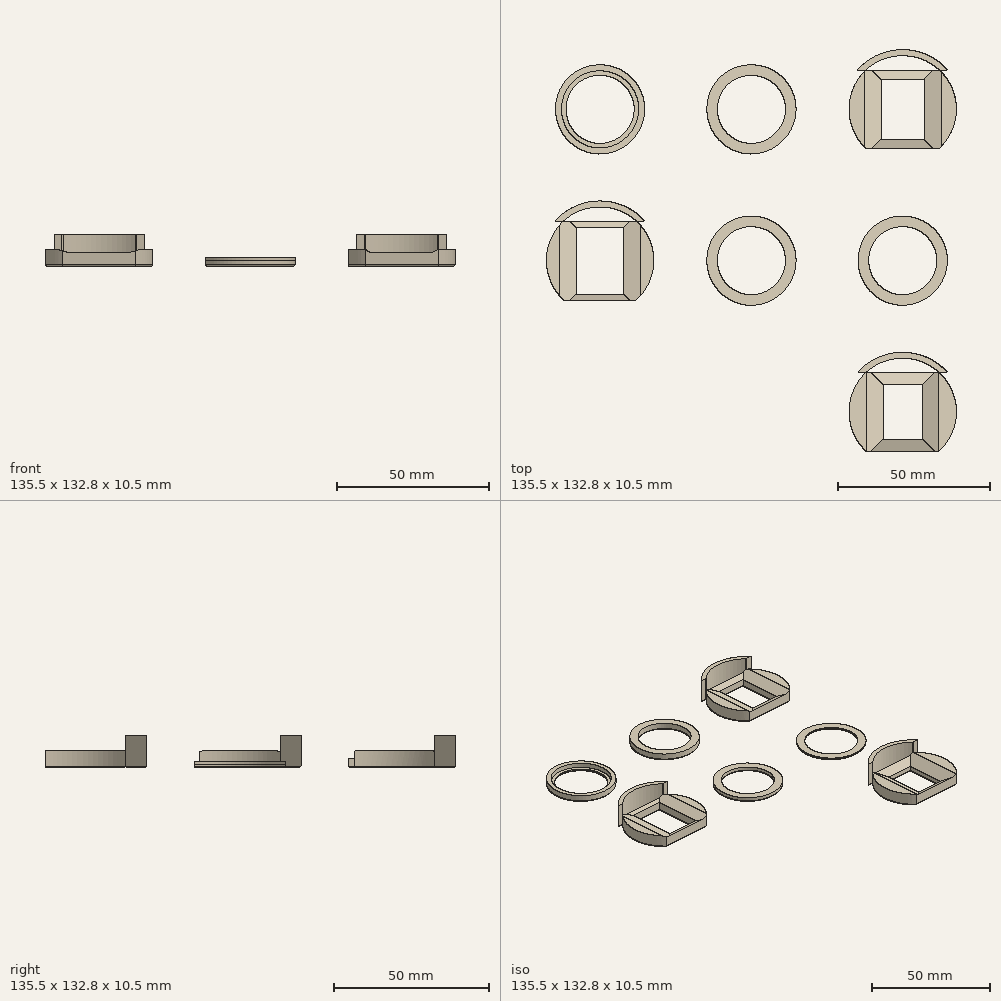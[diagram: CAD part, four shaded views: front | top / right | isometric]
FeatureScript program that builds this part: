
annotation { "Feature Type Name" : "Feature", "Feature Type Description" : "" }
export const myFeature = defineFeature(function(context is Context, id is Id, definition is map)
    precondition{}
    {
        {
            var Q0;
            Q0=qCreatedBy(makeId("Top.planeOp"),FACE);
            var sketch = newSketch(context, id + "F0", { "sketchPlane" : qUnion([Q0])});
            skCircle(sketch, "E0", {"center": v(-61.15, 61.18) * mm, "radius": 11.25 * mm});
            skCircle(sketch, "E1", {"center": v(-61.15, 61.18) * mm, "radius": 14.75 * mm});
            skLineSegment(sketch, "E2.bottom", {"start": v(-69.03, 22.18) * mm, "end": v(-53.28, 22.18) * mm});
            skLineSegment(sketch, "E2.top", {"start": v(-69.03, 0.18) * mm, "end": v(-53.28, 0.18) * mm});
            skLineSegment(sketch, "E2.left", {"start": v(-69.03, 22.18) * mm, "end": v(-69.03, 0.18) * mm});
            skLineSegment(sketch, "E2.right", {"start": v(-53.28, 22.18) * mm, "end": v(-53.28, 0.18) * mm});
            skLineSegment(sketch, "E3", {"start": v(-69.03, 0.18) * mm, "end": v(-53.28, 22.18) * mm, "construction": true});
            skCircle(sketch, "E4", {"center": v(-61.15, 11.18) * mm, "radius": 17.75 * mm});
            skCircle(sketch, "E5", {"center": v(-61.15, 11.18) * mm, "radius": 19.75 * mm});
            skCircle(sketch, "E6", {"center": v(-61.15, 61.18) * mm, "radius": 12.75 * mm});
            skLineSegment(sketch, "E7", {"start": v(-76.02, 24.18) * mm, "end": v(-46.29, 24.18) * mm});
            skLineSegment(sketch, "E8", {"start": v(-76.02, -1.82) * mm, "end": v(-46.29, -1.82) * mm});
            skCircle(sketch, "E9", {"center": v(-11.15, 61.18) * mm, "radius": 11.25 * mm});
            skCircle(sketch, "E10", {"center": v(-11.15, 61.18) * mm, "radius": 14.75 * mm});
            skCircle(sketch, "E11", {"center": v(-11.15, 11.18) * mm, "radius": 11.25 * mm});
            skCircle(sketch, "E12", {"center": v(-11.15, 11.18) * mm, "radius": 14.75 * mm});
            skCircle(sketch, "E13", {"center": v(38.85, 11.18) * mm, "radius": 11.25 * mm});
            skCircle(sketch, "E14", {"center": v(38.85, 11.18) * mm, "radius": 14.75 * mm});
            skLineSegment(sketch, "E15.bottom", {"start": v(31.69, 71.18) * mm, "end": v(46, 71.18) * mm});
            skLineSegment(sketch, "E15.top", {"start": v(31.69, 51.18) * mm, "end": v(46, 51.18) * mm});
            skLineSegment(sketch, "E15.left", {"start": v(31.69, 71.18) * mm, "end": v(31.69, 51.18) * mm});
            skLineSegment(sketch, "E15.right", {"start": v(46, 71.18) * mm, "end": v(46, 51.18) * mm});
            skLineSegment(sketch, "E16", {"start": v(31.69, 51.18) * mm, "end": v(46, 71.18) * mm, "construction": true});
            skCircle(sketch, "E17", {"center": v(38.85, 61.18) * mm, "radius": 17.75 * mm});
            skCircle(sketch, "E18", {"center": v(38.85, 61.18) * mm, "radius": 19.75 * mm});
            skLineSegment(sketch, "E19", {"start": v(23.98, 74.18) * mm, "end": v(53.71, 74.18) * mm});
            skLineSegment(sketch, "E20", {"start": v(23.98, 48.18) * mm, "end": v(53.71, 48.18) * mm});
            skLineSegment(sketch, "E21.bottom", {"start": v(32.4, -29.82) * mm, "end": v(45.29, -29.82) * mm});
            skLineSegment(sketch, "E21.top", {"start": v(32.4, -47.82) * mm, "end": v(45.29, -47.82) * mm});
            skLineSegment(sketch, "E21.left", {"start": v(32.4, -29.82) * mm, "end": v(32.4, -47.82) * mm});
            skLineSegment(sketch, "E21.right", {"start": v(45.29, -29.82) * mm, "end": v(45.29, -47.82) * mm});
            skLineSegment(sketch, "E22", {"start": v(32.4, -47.82) * mm, "end": v(45.29, -29.82) * mm, "construction": true});
            skCircle(sketch, "E23", {"center": v(38.85, -38.82) * mm, "radius": 17.75 * mm});
            skCircle(sketch, "E24", {"center": v(38.85, -38.82) * mm, "radius": 19.75 * mm});
            skLineSegment(sketch, "E25", {"start": v(23.98, -25.82) * mm, "end": v(53.71, -25.82) * mm});
            skLineSegment(sketch, "E26", {"start": v(23.98, -51.82) * mm, "end": v(53.71, -51.82) * mm});
            skSolve(sketch);
        }
        {
            var Q0;
            Q0=makeQuery(id+"F0.imprint","IMPRINT",FACE,{"disambiguationData":[TD([[makeQuery(id+"F0.imprint","IMPRINT",EDGE,{"derivedFrom":sQuery(id+"F0.wireOp",EDGE,"E0")}),-1.0]])]});
            extrude(context, id + "F1", {"entities" : qUnion([Q0]), "depth" : 1 * mm, "offsetDistance" : 25 * mm});
        }
        {
            var Q0;
            Q0=makeQuery(id+"F0.imprint","IMPRINT",FACE,{"disambiguationData":[TD([[makeQuery(id+"F0.imprint","IMPRINT",EDGE,{"derivedFrom":sQuery(id+"F0.wireOp",EDGE,"E1")}),1.0]])]});
            extrude(context, id + "F2", {"entities" : qUnion([Q0]), "operationType" : NewBodyOperationType.ADD, "depth" : 3 * mm, "offsetDistance" : 25 * mm});
        }
        {
            var Q0;
            Q0=makeQuery(id+"F0.imprint","IMPRINT",FACE,{"disambiguationData":[TD([[makeQuery(id+"F0.imprint","IMPRINT",EDGE,{"derivedFrom":sQuery(id+"F0.wireOp",EDGE,"E2.bottom")}),1.0]])]});
            var Q1;
            Q1=makeQuery(id+"F0.imprint","IMPRINT",FACE,{"disambiguationData":[TD([[makeQuery(id+"F0.imprint","IMPRINT",EDGE,{"derivedFrom":sQuery(id+"F0.wireOp",EDGE,"E15.bottom")}),1.0]])]});
            var Q2;
            Q2=makeQuery(id+"F0.imprint","IMPRINT",FACE,{"disambiguationData":[TD([[makeQuery(id+"F0.imprint","IMPRINT",EDGE,{"derivedFrom":sQuery(id+"F0.wireOp",EDGE,"E21.bottom")}),1.0]])]});
            extrude(context, id + "F3", {"entities" : qUnion([Q0, Q1, Q2]), "depth" : 5.5 * mm, "offsetDistance" : 25 * mm});
        }
        {
            var Q0;
            {var subQ0=sQuery(id+"F0.wireOp",EDGE,"E7");var subQ1=sQuery(id+"F0.wireOp",EDGE,"E4");var subQ2=makeQuery(id+"F0.imprint","INTERSECT",VERTEX,{"disambiguationData":[OD(0.0)],"derivedFrom":[subQ1,subQ0]});Q0=makeQuery(id+"F0.imprint","IMPRINT",FACE,{"disambiguationData":[TD([[makeQuery(id+"F0.imprint","IMPRINT",EDGE,{"disambiguationData":[TD([[subQ2,-1.0]])],"derivedFrom":subQ1}),-1.0]])]});}
            var Q1;
            {var subQ0=sQuery(id+"F0.wireOp",EDGE,"E7");var subQ1=sQuery(id+"F0.wireOp",EDGE,"E4");var subQ2=makeQuery(id+"F0.imprint","INTERSECT",VERTEX,{"disambiguationData":[OD(1.0)],"derivedFrom":[subQ1,subQ0]});Q1=makeQuery(id+"F0.imprint","IMPRINT",FACE,{"disambiguationData":[TD([[makeQuery(id+"F0.imprint","IMPRINT",EDGE,{"disambiguationData":[TD([[subQ2,1.0]])],"derivedFrom":subQ1}),-1.0]])]});}
            var Q2;
            {var subQ0=sQuery(id+"F0.wireOp",EDGE,"E19");var subQ1=sQuery(id+"F0.wireOp",EDGE,"E17");var subQ2=makeQuery(id+"F0.imprint","INTERSECT",VERTEX,{"disambiguationData":[OD(0.0)],"derivedFrom":[subQ1,subQ0]});Q2=makeQuery(id+"F0.imprint","IMPRINT",FACE,{"disambiguationData":[TD([[makeQuery(id+"F0.imprint","IMPRINT",EDGE,{"disambiguationData":[TD([[subQ2,-1.0]])],"derivedFrom":subQ1}),-1.0]])]});}
            var Q3;
            {var subQ0=sQuery(id+"F0.wireOp",EDGE,"E19");var subQ1=sQuery(id+"F0.wireOp",EDGE,"E17");var subQ2=makeQuery(id+"F0.imprint","INTERSECT",VERTEX,{"disambiguationData":[OD(1.0)],"derivedFrom":[subQ1,subQ0]});Q3=makeQuery(id+"F0.imprint","IMPRINT",FACE,{"disambiguationData":[TD([[makeQuery(id+"F0.imprint","IMPRINT",EDGE,{"disambiguationData":[TD([[subQ2,1.0]])],"derivedFrom":subQ1}),-1.0]])]});}
            var Q4;
            {var subQ0=sQuery(id+"F0.wireOp",EDGE,"E25");var subQ1=sQuery(id+"F0.wireOp",EDGE,"E23");var subQ2=makeQuery(id+"F0.imprint","INTERSECT",VERTEX,{"disambiguationData":[OD(0.0)],"derivedFrom":[subQ1,subQ0]});Q4=makeQuery(id+"F0.imprint","IMPRINT",FACE,{"disambiguationData":[TD([[makeQuery(id+"F0.imprint","IMPRINT",EDGE,{"disambiguationData":[TD([[subQ2,-1.0]])],"derivedFrom":subQ1}),-1.0]])]});}
            var Q5;
            {var subQ0=sQuery(id+"F0.wireOp",EDGE,"E25");var subQ1=sQuery(id+"F0.wireOp",EDGE,"E23");var subQ2=makeQuery(id+"F0.imprint","INTERSECT",VERTEX,{"disambiguationData":[OD(1.0)],"derivedFrom":[subQ1,subQ0]});Q5=makeQuery(id+"F0.imprint","IMPRINT",FACE,{"disambiguationData":[TD([[makeQuery(id+"F0.imprint","IMPRINT",EDGE,{"disambiguationData":[TD([[subQ2,1.0]])],"derivedFrom":subQ1}),-1.0]])]});}
            extrude(context, id + "F4", {"entities" : qUnion([Q0, Q1, Q2, Q3, Q4, Q5]), "operationType" : NewBodyOperationType.ADD, "depth" : 10.5 * mm, "offsetDistance" : 25 * mm});
        }
        {
            var Q0;
            Q0=makeQuery(id+"F0.imprint","IMPRINT",FACE,{"disambiguationData":[TD([[makeQuery(id+"F0.imprint","IMPRINT",EDGE,{"derivedFrom":sQuery(id+"F0.wireOp",EDGE,"E10")}),1.0]])]});
            extrude(context, id + "F5", {"entities" : qUnion([Q0]), "depth" : 3 * mm, "offsetDistance" : 25 * mm});
        }
        {
            var Q0;
            Q0=makeQuery(id+"F0.imprint","IMPRINT",FACE,{"disambiguationData":[TD([[makeQuery(id+"F0.imprint","IMPRINT",EDGE,{"derivedFrom":sQuery(id+"F0.wireOp",EDGE,"E11")}),-1.0]])]});
            extrude(context, id + "F6", {"entities" : qUnion([Q0]), "operationType" : NewBodyOperationType.ADD, "depth" : 2 * mm, "offsetDistance" : 25 * mm});
        }
        {
            var Q0;
            Q0=makeQuery(id+"F0.imprint","IMPRINT",FACE,{"disambiguationData":[TD([[makeQuery(id+"F0.imprint","IMPRINT",EDGE,{"derivedFrom":sQuery(id+"F0.wireOp",EDGE,"E14")}),1.0]])]});
            extrude(context, id + "F7", {"entities" : qUnion([Q0]), "depth" : 1 * mm, "offsetDistance" : 25 * mm});
        }
        {
            var Q0;
            Q0=makeQuery(id+"F3.opExtrude","CAP_EDGE",EDGE,{"disambiguationData":[OSD([sQuery(id+"F0.wireOp",EDGE,"E2.bottom")])],"isStart":false});
            var Q1;
            Q1=makeQuery(id+"F3.opExtrude","CAP_EDGE",EDGE,{"disambiguationData":[OSD([sQuery(id+"F0.wireOp",EDGE,"E2.right")])],"isStart":false});
            var Q2;
            Q2=makeQuery(id+"F3.opExtrude","CAP_EDGE",EDGE,{"disambiguationData":[OSD([sQuery(id+"F0.wireOp",EDGE,"E2.top")])],"isStart":false});
            var Q3;
            Q3=makeQuery(id+"F3.opExtrude","CAP_EDGE",EDGE,{"disambiguationData":[OSD([sQuery(id+"F0.wireOp",EDGE,"E2.left")])],"isStart":false});
            chamfer(context, id + "F8", {"entities" : qUnion([Q0, Q1, Q2, Q3]), "chamferType" : ChamferType.TWO_OFFSETS, "width1" : 1.6 * mm, "oppositeDirection" : false, "width2" : 5.5 * mm, "tangentPropagation" : true});
        }
        {
            var Q0;
            {var subQ0=sQuery(id+"F0.wireOp",EDGE,"E8");var subQ1=sQuery(id+"F0.wireOp",EDGE,"E5");var subQ2=makeQuery(id+"F0.imprint","INTERSECT",VERTEX,{"disambiguationData":[OD(1.0)],"derivedFrom":[subQ1,subQ0]});var subQ3=sQuery(id+"F0.wireOp",EDGE,"E4");var subQ5=sQuery(id+"F0.wireOp",EDGE,"E7");var subQ6=makeQuery(id+"F0.imprint","INTERSECT",VERTEX,{"disambiguationData":[OD(1.0)],"derivedFrom":[subQ1,subQ5]});var subQ7=makeQuery(id+"F0.imprint","INTERSECT",VERTEX,{"disambiguationData":[OD(1.0)],"derivedFrom":[subQ3,subQ5]});var subQ8=makeQuery(id+"F0.imprint","INTERSECT",VERTEX,{"disambiguationData":[OD(0.0)],"derivedFrom":[subQ1,subQ0]});var subQ10=makeQuery(id+"F0.imprint","INTERSECT",VERTEX,{"disambiguationData":[OD(0.0)],"derivedFrom":[subQ1,subQ5]});var subQ11=makeQuery(id+"F0.imprint","INTERSECT",VERTEX,{"disambiguationData":[OD(0.0)],"derivedFrom":[subQ3,subQ5]});Q0=makeQuery(id+"F4.boolean.opBoolean","MERGE",FACE,{"derivedFrom":[makeQuery(id+"F3.opExtrude","CAP_FACE",FACE,{"disambiguationData":[OSD([sQuery(id+"F0.wireOp",EDGE,"E2.bottom"),sQuery(id+"F0.wireOp",EDGE,"E2.top"),sQuery(id+"F0.wireOp",EDGE,"E2.left"),sQuery(id+"F0.wireOp",EDGE,"E2.right"),subQ3,subQ5,subQ0])],"isStart":true}),makeQuery(id+"F4.opExtrude","CAP_FACE",FACE,{"disambiguationData":[OSD([subQ3,subQ1,subQ5,subQ0]),TDD([makeQuery(id+"F0.imprint","IMPRINT",EDGE,{"disambiguationData":[TD([[subQ11,-1.0]])],"derivedFrom":subQ3}),makeQuery(id+"F0.imprint","IMPRINT",EDGE,{"disambiguationData":[TD([[subQ10,-1.0]])],"derivedFrom":subQ1}),makeQuery(id+"F0.imprint","IMPRINT",EDGE,{"disambiguationData":[TD([[subQ10,-1.0]])],"derivedFrom":subQ5}),makeQuery(id+"F0.imprint","IMPRINT",EDGE,{"disambiguationData":[TD([[subQ8,-1.0]])],"derivedFrom":subQ0})])],"isStart":true}),makeQuery(id+"F4.opExtrude","CAP_FACE",FACE,{"disambiguationData":[OSD([subQ3,subQ1,subQ5,subQ0]),TDD([makeQuery(id+"F0.imprint","IMPRINT",EDGE,{"disambiguationData":[TD([[subQ7,1.0]])],"derivedFrom":subQ3}),makeQuery(id+"F0.imprint","IMPRINT",EDGE,{"disambiguationData":[TD([[subQ6,1.0]])],"derivedFrom":subQ1}),makeQuery(id+"F0.imprint","IMPRINT",EDGE,{"disambiguationData":[TD([[subQ6,1.0]])],"derivedFrom":subQ5}),makeQuery(id+"F0.imprint","IMPRINT",EDGE,{"disambiguationData":[TD([[subQ2,1.0]])],"derivedFrom":subQ0})])],"isStart":true})]});}
            var Q1;
            {var subQ0=sQuery(id+"F0.wireOp",EDGE,"E6");Q1=makeQuery(id+"F2.boolean.opBoolean","MERGE",FACE,{"derivedFrom":[makeQuery(id+"F1.opExtrude","CAP_FACE",FACE,{"disambiguationData":[OSD([sQuery(id+"F0.wireOp",EDGE,"E0"),subQ0])],"isStart":true}),makeQuery(id+"F2.opExtrude","CAP_FACE",FACE,{"disambiguationData":[OSD([sQuery(id+"F0.wireOp",EDGE,"E1"),subQ0])],"isStart":true})]});}
            var Q2;
            Q2=makeQuery(id+"F5.opExtrude","CAP_FACE",FACE,{"disambiguationData":[OSD([sQuery(id+"F0.wireOp",EDGE,"E9"),sQuery(id+"F0.wireOp",EDGE,"E10")])],"isStart":true});
            var Q3;
            {var subQ0=sQuery(id+"F0.wireOp",EDGE,"E8");var subQ1=sQuery(id+"F0.wireOp",EDGE,"E4");Q3=makeQuery(id+"F4.opExtrude","SWEPT_EDGE",EDGE,{"disambiguationData":[OSD([subQ1,subQ0]),TDD([makeQuery(id+"F0.imprint","INTERSECT",VERTEX,{"disambiguationData":[OD(1.0)],"derivedFrom":[subQ1,subQ0]})])]});}
            var Q4;
            {var subQ0=sQuery(id+"F0.wireOp",EDGE,"E7");var subQ1=sQuery(id+"F0.wireOp",EDGE,"E4");Q4=makeQuery(id+"F4.opExtrude","SWEPT_EDGE",EDGE,{"disambiguationData":[OSD([subQ1,subQ0]),TDD([makeQuery(id+"F0.imprint","INTERSECT",VERTEX,{"disambiguationData":[OD(1.0)],"derivedFrom":[subQ1,subQ0]})])]});}
            var Q5;
            {var subQ0=sQuery(id+"F0.wireOp",EDGE,"E7");var subQ1=sQuery(id+"F0.wireOp",EDGE,"E4");Q5=makeQuery(id+"F4.opExtrude","SWEPT_EDGE",EDGE,{"disambiguationData":[OSD([subQ1,subQ0]),TDD([makeQuery(id+"F0.imprint","INTERSECT",VERTEX,{"disambiguationData":[OD(0.0)],"derivedFrom":[subQ1,subQ0]})])]});}
            var Q6;
            {var subQ0=sQuery(id+"F0.wireOp",EDGE,"E8");var subQ1=sQuery(id+"F0.wireOp",EDGE,"E4");Q6=makeQuery(id+"F4.opExtrude","SWEPT_EDGE",EDGE,{"disambiguationData":[OSD([subQ1,subQ0]),TDD([makeQuery(id+"F0.imprint","INTERSECT",VERTEX,{"disambiguationData":[OD(0.0)],"derivedFrom":[subQ1,subQ0]})])]});}
            var Q7;
            Q7=makeQuery(id+"F7.opExtrude","CAP_FACE",FACE,{"disambiguationData":[OSD([sQuery(id+"F0.wireOp",EDGE,"E13"),sQuery(id+"F0.wireOp",EDGE,"E14")])],"isStart":true});
            var Q8;
            {var subQ0=sQuery(id+"F0.wireOp",EDGE,"E20");var subQ1=sQuery(id+"F0.wireOp",EDGE,"E18");var subQ2=makeQuery(id+"F0.imprint","INTERSECT",VERTEX,{"disambiguationData":[OD(1.0)],"derivedFrom":[subQ1,subQ0]});var subQ3=sQuery(id+"F0.wireOp",EDGE,"E17");var subQ5=sQuery(id+"F0.wireOp",EDGE,"E19");var subQ6=makeQuery(id+"F0.imprint","INTERSECT",VERTEX,{"disambiguationData":[OD(1.0)],"derivedFrom":[subQ1,subQ5]});var subQ7=makeQuery(id+"F0.imprint","INTERSECT",VERTEX,{"disambiguationData":[OD(1.0)],"derivedFrom":[subQ3,subQ5]});var subQ8=makeQuery(id+"F0.imprint","INTERSECT",VERTEX,{"disambiguationData":[OD(0.0)],"derivedFrom":[subQ1,subQ0]});var subQ10=makeQuery(id+"F0.imprint","INTERSECT",VERTEX,{"disambiguationData":[OD(0.0)],"derivedFrom":[subQ1,subQ5]});var subQ11=makeQuery(id+"F0.imprint","INTERSECT",VERTEX,{"disambiguationData":[OD(0.0)],"derivedFrom":[subQ3,subQ5]});Q8=makeQuery(id+"F6.boolean.opBoolean","MERGE",FACE,{"derivedFrom":[makeQuery(id+"F3.opExtrude","CAP_FACE",FACE,{"disambiguationData":[OSD([sQuery(id+"F0.wireOp",EDGE,"E15.bottom"),sQuery(id+"F0.wireOp",EDGE,"E15.top"),sQuery(id+"F0.wireOp",EDGE,"E15.left"),sQuery(id+"F0.wireOp",EDGE,"E15.right"),subQ3,subQ5,subQ0])],"isStart":true}),makeQuery(id+"F4.opExtrude","CAP_FACE",FACE,{"disambiguationData":[OSD([subQ3,subQ1,subQ5,subQ0]),TDD([makeQuery(id+"F0.imprint","IMPRINT",EDGE,{"disambiguationData":[TD([[subQ11,-1.0]])],"derivedFrom":subQ3}),makeQuery(id+"F0.imprint","IMPRINT",EDGE,{"disambiguationData":[TD([[subQ10,-1.0]])],"derivedFrom":subQ1}),makeQuery(id+"F0.imprint","IMPRINT",EDGE,{"disambiguationData":[TD([[subQ10,-1.0]])],"derivedFrom":subQ5}),makeQuery(id+"F0.imprint","IMPRINT",EDGE,{"disambiguationData":[TD([[subQ8,-1.0]])],"derivedFrom":subQ0})])],"isStart":true}),makeQuery(id+"F4.opExtrude","CAP_FACE",FACE,{"disambiguationData":[OSD([subQ3,subQ1,subQ5,subQ0]),TDD([makeQuery(id+"F0.imprint","IMPRINT",EDGE,{"disambiguationData":[TD([[subQ7,1.0]])],"derivedFrom":subQ3}),makeQuery(id+"F0.imprint","IMPRINT",EDGE,{"disambiguationData":[TD([[subQ6,1.0]])],"derivedFrom":subQ1}),makeQuery(id+"F0.imprint","IMPRINT",EDGE,{"disambiguationData":[TD([[subQ6,1.0]])],"derivedFrom":subQ5}),makeQuery(id+"F0.imprint","IMPRINT",EDGE,{"disambiguationData":[TD([[subQ2,1.0]])],"derivedFrom":subQ0})])],"isStart":true})]});}
            var Q9;
            {var subQ0=sQuery(id+"F0.wireOp",EDGE,"E20");var subQ1=sQuery(id+"F0.wireOp",EDGE,"E17");Q9=makeQuery(id+"F4.opExtrude","SWEPT_EDGE",EDGE,{"disambiguationData":[OSD([subQ1,subQ0]),TDD([makeQuery(id+"F0.imprint","INTERSECT",VERTEX,{"disambiguationData":[OD(0.0)],"derivedFrom":[subQ1,subQ0]})])]});}
            var Q10;
            {var subQ0=sQuery(id+"F0.wireOp",EDGE,"E19");var subQ1=sQuery(id+"F0.wireOp",EDGE,"E17");Q10=makeQuery(id+"F4.opExtrude","SWEPT_EDGE",EDGE,{"disambiguationData":[OSD([subQ1,subQ0]),TDD([makeQuery(id+"F0.imprint","INTERSECT",VERTEX,{"disambiguationData":[OD(0.0)],"derivedFrom":[subQ1,subQ0]})])]});}
            var Q11;
            {var subQ0=sQuery(id+"F0.wireOp",EDGE,"E19");var subQ1=sQuery(id+"F0.wireOp",EDGE,"E17");Q11=makeQuery(id+"F4.opExtrude","SWEPT_EDGE",EDGE,{"disambiguationData":[OSD([subQ1,subQ0]),TDD([makeQuery(id+"F0.imprint","INTERSECT",VERTEX,{"disambiguationData":[OD(1.0)],"derivedFrom":[subQ1,subQ0]})])]});}
            var Q12;
            {var subQ0=sQuery(id+"F0.wireOp",EDGE,"E20");var subQ1=sQuery(id+"F0.wireOp",EDGE,"E17");Q12=makeQuery(id+"F4.opExtrude","SWEPT_EDGE",EDGE,{"disambiguationData":[OSD([subQ1,subQ0]),TDD([makeQuery(id+"F0.imprint","INTERSECT",VERTEX,{"disambiguationData":[OD(1.0)],"derivedFrom":[subQ1,subQ0]})])]});}
            var Q13;
            Q13=makeQuery(id+"F6.opExtrude","CAP_FACE",FACE,{"disambiguationData":[OSD([sQuery(id+"F0.wireOp",EDGE,"E11"),sQuery(id+"F0.wireOp",EDGE,"E12")])],"isStart":true});
            var Q14;
            {var subQ0=sQuery(id+"F0.wireOp",EDGE,"E26");var subQ1=sQuery(id+"F0.wireOp",EDGE,"E24");var subQ2=makeQuery(id+"F0.imprint","INTERSECT",VERTEX,{"disambiguationData":[OD(1.0)],"derivedFrom":[subQ1,subQ0]});var subQ3=sQuery(id+"F0.wireOp",EDGE,"E23");var subQ5=sQuery(id+"F0.wireOp",EDGE,"E25");var subQ6=makeQuery(id+"F0.imprint","INTERSECT",VERTEX,{"disambiguationData":[OD(1.0)],"derivedFrom":[subQ1,subQ5]});var subQ7=makeQuery(id+"F0.imprint","INTERSECT",VERTEX,{"disambiguationData":[OD(1.0)],"derivedFrom":[subQ3,subQ5]});var subQ8=makeQuery(id+"F0.imprint","INTERSECT",VERTEX,{"disambiguationData":[OD(0.0)],"derivedFrom":[subQ1,subQ0]});var subQ10=makeQuery(id+"F0.imprint","INTERSECT",VERTEX,{"disambiguationData":[OD(0.0)],"derivedFrom":[subQ1,subQ5]});var subQ11=makeQuery(id+"F0.imprint","INTERSECT",VERTEX,{"disambiguationData":[OD(0.0)],"derivedFrom":[subQ3,subQ5]});Q14=makeQuery(id+"F6.boolean.opBoolean","MERGE",FACE,{"derivedFrom":[makeQuery(id+"F3.opExtrude","CAP_FACE",FACE,{"disambiguationData":[OSD([sQuery(id+"F0.wireOp",EDGE,"E21.bottom"),sQuery(id+"F0.wireOp",EDGE,"E21.top"),sQuery(id+"F0.wireOp",EDGE,"E21.left"),sQuery(id+"F0.wireOp",EDGE,"E21.right"),subQ3,subQ5,subQ0])],"isStart":true}),makeQuery(id+"F4.opExtrude","CAP_FACE",FACE,{"disambiguationData":[OSD([subQ3,subQ1,subQ5,subQ0]),TDD([makeQuery(id+"F0.imprint","IMPRINT",EDGE,{"disambiguationData":[TD([[subQ11,-1.0]])],"derivedFrom":subQ3}),makeQuery(id+"F0.imprint","IMPRINT",EDGE,{"disambiguationData":[TD([[subQ10,-1.0]])],"derivedFrom":subQ1}),makeQuery(id+"F0.imprint","IMPRINT",EDGE,{"disambiguationData":[TD([[subQ10,-1.0]])],"derivedFrom":subQ5}),makeQuery(id+"F0.imprint","IMPRINT",EDGE,{"disambiguationData":[TD([[subQ8,-1.0]])],"derivedFrom":subQ0})])],"isStart":true}),makeQuery(id+"F4.opExtrude","CAP_FACE",FACE,{"disambiguationData":[OSD([subQ3,subQ1,subQ5,subQ0]),TDD([makeQuery(id+"F0.imprint","IMPRINT",EDGE,{"disambiguationData":[TD([[subQ7,1.0]])],"derivedFrom":subQ3}),makeQuery(id+"F0.imprint","IMPRINT",EDGE,{"disambiguationData":[TD([[subQ6,1.0]])],"derivedFrom":subQ1}),makeQuery(id+"F0.imprint","IMPRINT",EDGE,{"disambiguationData":[TD([[subQ6,1.0]])],"derivedFrom":subQ5}),makeQuery(id+"F0.imprint","IMPRINT",EDGE,{"disambiguationData":[TD([[subQ2,1.0]])],"derivedFrom":subQ0})])],"isStart":true})]});}
            var Q15;
            {var subQ0=sQuery(id+"F0.wireOp",EDGE,"E25");var subQ1=sQuery(id+"F0.wireOp",EDGE,"E23");Q15=makeQuery(id+"F4.opExtrude","SWEPT_EDGE",EDGE,{"disambiguationData":[OSD([subQ1,subQ0]),TDD([makeQuery(id+"F0.imprint","INTERSECT",VERTEX,{"disambiguationData":[OD(0.0)],"derivedFrom":[subQ1,subQ0]})])]});}
            var Q16;
            {var subQ0=sQuery(id+"F0.wireOp",EDGE,"E26");var subQ1=sQuery(id+"F0.wireOp",EDGE,"E23");Q16=makeQuery(id+"F4.opExtrude","SWEPT_EDGE",EDGE,{"disambiguationData":[OSD([subQ1,subQ0]),TDD([makeQuery(id+"F0.imprint","INTERSECT",VERTEX,{"disambiguationData":[OD(0.0)],"derivedFrom":[subQ1,subQ0]})])]});}
            var Q17;
            {var subQ0=sQuery(id+"F0.wireOp",EDGE,"E26");var subQ1=sQuery(id+"F0.wireOp",EDGE,"E23");Q17=makeQuery(id+"F4.opExtrude","SWEPT_EDGE",EDGE,{"disambiguationData":[OSD([subQ1,subQ0]),TDD([makeQuery(id+"F0.imprint","INTERSECT",VERTEX,{"disambiguationData":[OD(1.0)],"derivedFrom":[subQ1,subQ0]})])]});}
            var Q18;
            {var subQ0=sQuery(id+"F0.wireOp",EDGE,"E25");var subQ1=sQuery(id+"F0.wireOp",EDGE,"E23");Q18=makeQuery(id+"F4.opExtrude","SWEPT_EDGE",EDGE,{"disambiguationData":[OSD([subQ1,subQ0]),TDD([makeQuery(id+"F0.imprint","INTERSECT",VERTEX,{"disambiguationData":[OD(1.0)],"derivedFrom":[subQ1,subQ0]})])]});}
            fillet(context, id + "F9", {"entities" : qUnion([Q0, Q1, Q2, Q3, Q4, Q5, Q6, Q7, Q8, Q9, Q10, Q11, Q12, Q13, Q14, Q15, Q16, Q17, Q18]), "radius" : .5 * mm, "tangentPropagation" : true, "allowEdgeOverflow" : false});
        }
        {
            var Q0;
            Q0=makeQuery(id+"F3.opExtrude","CAP_EDGE",EDGE,{"disambiguationData":[OSD([sQuery(id+"F0.wireOp",EDGE,"E15.left")])],"isStart":false});
            var Q1;
            Q1=makeQuery(id+"F3.opExtrude","CAP_EDGE",EDGE,{"disambiguationData":[OSD([sQuery(id+"F0.wireOp",EDGE,"E15.bottom")])],"isStart":false});
            var Q2;
            Q2=makeQuery(id+"F3.opExtrude","CAP_EDGE",EDGE,{"disambiguationData":[OSD([sQuery(id+"F0.wireOp",EDGE,"E15.top")])],"isStart":false});
            var Q3;
            Q3=makeQuery(id+"F3.opExtrude","CAP_EDGE",EDGE,{"disambiguationData":[OSD([sQuery(id+"F0.wireOp",EDGE,"E15.right")])],"isStart":false});
            chamfer(context, id + "F10", {"entities" : qUnion([Q0, Q1, Q2, Q3]), "chamferType" : ChamferType.TWO_OFFSETS, "width1" : 5.5 * mm, "oppositeDirection" : false, "width2" : 2 * mm, "tangentPropagation" : true});
        }
        {
            var Q0;
            Q0=makeQuery(id+"F3.opExtrude","CAP_EDGE",EDGE,{"disambiguationData":[OSD([sQuery(id+"F0.wireOp",EDGE,"E21.top")])],"isStart":false});
            var Q1;
            Q1=makeQuery(id+"F3.opExtrude","CAP_EDGE",EDGE,{"disambiguationData":[OSD([sQuery(id+"F0.wireOp",EDGE,"E21.right")])],"isStart":false});
            var Q2;
            Q2=makeQuery(id+"F3.opExtrude","CAP_EDGE",EDGE,{"disambiguationData":[OSD([sQuery(id+"F0.wireOp",EDGE,"E21.bottom")])],"isStart":false});
            var Q3;
            Q3=makeQuery(id+"F3.opExtrude","CAP_EDGE",EDGE,{"disambiguationData":[OSD([sQuery(id+"F0.wireOp",EDGE,"E21.left")])],"isStart":false});
            chamfer(context, id + "F11", {"entities" : qUnion([Q0, Q1, Q2, Q3]), "chamferType" : ChamferType.TWO_OFFSETS, "width1" : 5.5 * mm, "oppositeDirection" : false, "width2" : 3 * mm, "tangentPropagation" : true});
        }
    });
